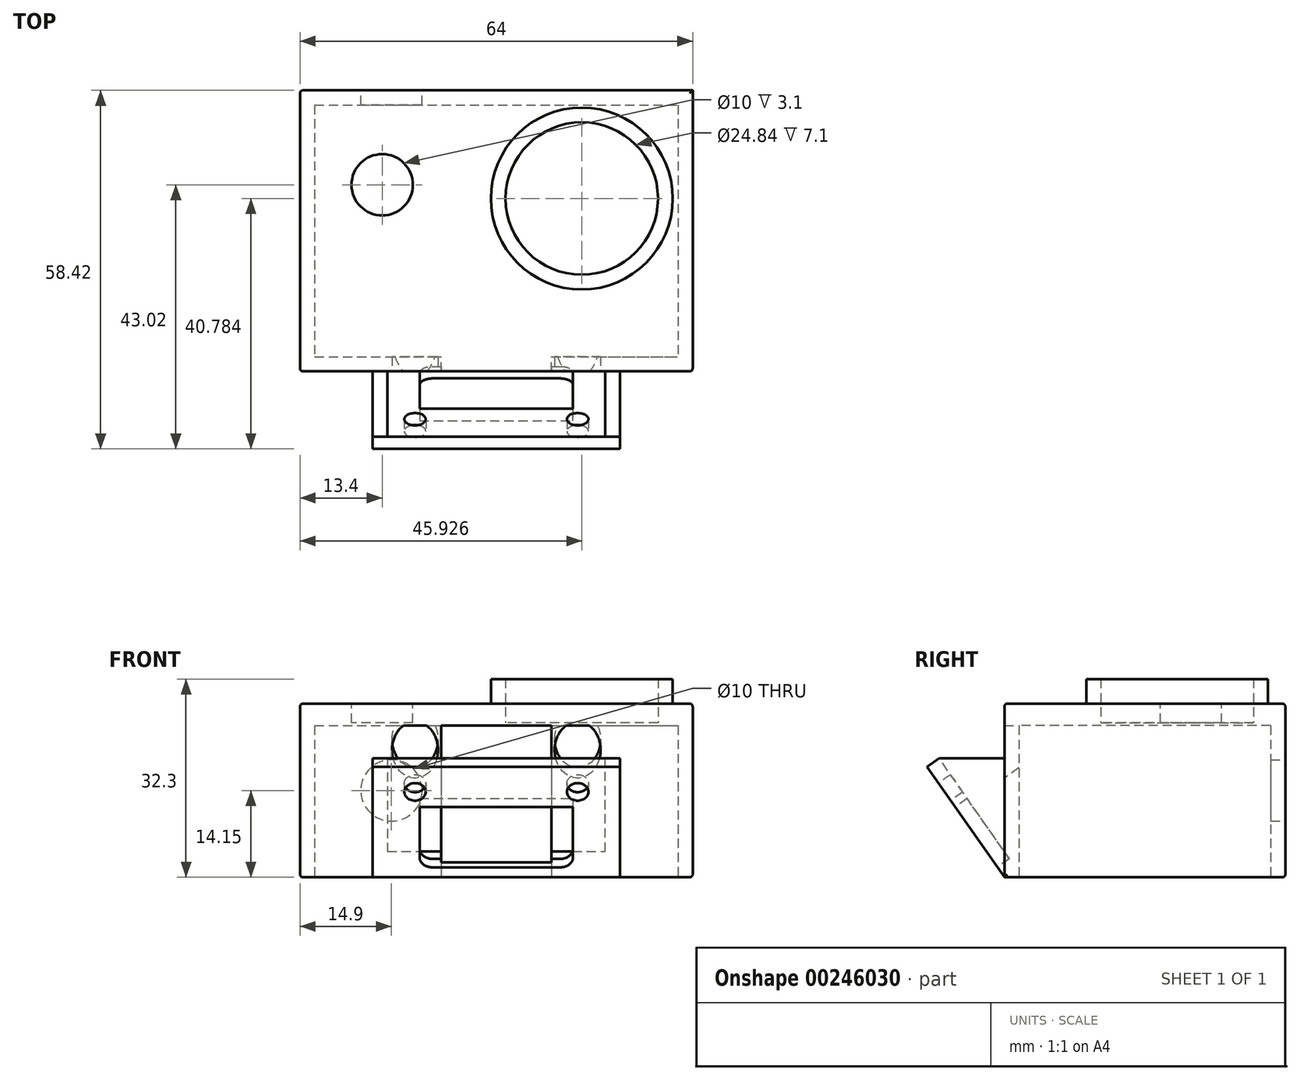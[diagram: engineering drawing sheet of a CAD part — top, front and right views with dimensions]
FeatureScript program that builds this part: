
annotation { "Feature Type Name" : "Feature", "Feature Type Description" : "" }
export const myFeature = defineFeature(function(context is Context, id is Id, definition is map)
    precondition{}
    {
        {
            assignVariable(context, id + "F0", {"name" : "goproThickness", "anyValue" : 24.7});
        }
        {
            assignVariable(context, id + "F1", {"name" : "lensDepth", "anyValue" : 4});
        }
        {
            assignVariable(context, id + "F2", {"name" : "caseThickness", "anyValue" : 2.4});
        }
        {
            assignVariable(context, id + "F3", {"name" : "webThickness", "anyValue" : 0.5});
        }
        {
            assignVariable(context, id + "F4", {"name" : "cameraTilt", "anyValue" : 35});
        }
        {
            var Q0;
            Q0=qCreatedBy(makeId("Top.planeOp"),FACE);
            var sketch = newSketch(context, id + "F5", { "sketchPlane" : qUnion([Q0])});
            skLineSegment(sketch, "E0.bottom", {"start": v(-29.6, 20.5) * mm, "end": v(29.6, 20.5) * mm});
            skLineSegment(sketch, "E0.top", {"start": v(-29.6, -20.5) * mm, "end": v(29.6, -20.5) * mm});
            skLineSegment(sketch, "E0.left", {"start": v(-29.6, 20.5) * mm, "end": v(-29.6, -20.5) * mm});
            skLineSegment(sketch, "E0.right", {"start": v(29.6, 20.5) * mm, "end": v(29.6, -20.5) * mm});
            skPoint(sketch, "E0.middle", {"position": v(0, 0) * mm});
            skLineSegment(sketch, "E1.0", {"start": v(-32, 22.9) * mm, "end": v(32, 22.9) * mm});
            skLineSegment(sketch, "E1.1", {"start": v(-32, 22.9) * mm, "end": v(-32, -22.9) * mm});
            skLineSegment(sketch, "E1.2", {"start": v(-32, -22.9) * mm, "end": v(32, -22.9) * mm});
            skLineSegment(sketch, "E1.3", {"start": v(32, 22.9) * mm, "end": v(32, -22.9) * mm});
            skSolve(sketch);
        }
        {
            var Q0;
            Q0=qSketchRegion(id+"F5",true);
            extrude(context, id + "F6", {"entities" : qUnion([Q0]), "depth" : (getVariable(context, 'goproThickness')) * mm});
        }
        {
            var Q0;
            Q0=makeQuery(id+"F6.opExtrude","CAP_FACE",FACE,{"disambiguationData":[OSD([sQuery(id+"F5.wireOp",EDGE,"E0.bottom"),sQuery(id+"F5.wireOp",EDGE,"E0.top"),sQuery(id+"F5.wireOp",EDGE,"E0.left"),sQuery(id+"F5.wireOp",EDGE,"E0.right"),sQuery(id+"F5.wireOp",EDGE,"E1.0"),sQuery(id+"F5.wireOp",EDGE,"E1.1"),sQuery(id+"F5.wireOp",EDGE,"E1.2"),sQuery(id+"F5.wireOp",EDGE,"E1.3")])],"isStart":false});
            var sketch = newSketch(context, id + "F7", { "sketchPlane" : qUnion([Q0])});
            skLineSegment(sketch, "E2.bottom", {"start": v(-29.6, 20.5) * mm, "end": v(29.6, 20.5) * mm});
            skLineSegment(sketch, "E2.top", {"start": v(-29.6, -20.5) * mm, "end": v(29.6, -20.5) * mm});
            skLineSegment(sketch, "E2.left", {"start": v(-29.6, 20.5) * mm, "end": v(-29.6, -20.5) * mm});
            skLineSegment(sketch, "E2.right", {"start": v(29.6, 20.5) * mm, "end": v(29.6, -20.5) * mm});
            skPoint(sketch, "E2.middle", {"position": v(0, 0) * mm});
            skLineSegment(sketch, "E3.bottom", {"start": v(-32, 22.9) * mm, "end": v(32, 22.9) * mm});
            skLineSegment(sketch, "E3.top", {"start": v(-32, -22.9) * mm, "end": v(32, -22.9) * mm});
            skLineSegment(sketch, "E3.left", {"start": v(-32, 22.9) * mm, "end": v(-32, -22.9) * mm});
            skLineSegment(sketch, "E3.right", {"start": v(32, 22.9) * mm, "end": v(32, -22.9) * mm});
            skSolve(sketch);
        }
        {
            var Q0;
            Q0=qSketchRegion(id+"F7",true);
            var Q1;
            Q1=makeQuery(id+"F7.imprint","IMPRINT",FACE,{"disambiguationData":[TD([[makeQuery(id+"F7.imprint","IMPRINT",EDGE,{"derivedFrom":sQuery(id+"F7.wireOp",EDGE,"E2.bottom")}),-1.0]])]});
            extrude(context, id + "F8", {"entities" : qUnion([Q0, Q1]), "operationType" : NewBodyOperationType.ADD, "depth" : (getVariable(context, 'caseThickness') * 1.5) * mm});
        }
        {
            var Q0;
            Q0=makeQuery(id+"F8.opExtrude","CAP_FACE",FACE,{"disambiguationData":[OSD([sQuery(id+"F7.wireOp",EDGE,"E3.bottom"),sQuery(id+"F7.wireOp",EDGE,"E3.top"),sQuery(id+"F7.wireOp",EDGE,"E3.left"),sQuery(id+"F7.wireOp",EDGE,"E3.right")])],"isStart":false});
            var sketch = newSketch(context, id + "F9", { "sketchPlane" : qUnion([Q0])});
            skCircle(sketch, "E4", {"center": v(-18.6, 7.5) * mm, "radius": 5 * mm});
            skSolve(sketch);
        }
        {
            var Q0;
            Q0=qSketchRegion(id+"F9",true);
            extrude(context, id + "F10", {"entities" : qUnion([Q0]), "operationType" : NewBodyOperationType.REMOVE, "oppositeDirection" : true, "depth" : (getVariable(context, 'caseThickness') * 1.5 - getVariable(context, 'webThickness')) * mm});
        }
        {
            var Q0;
            Q0=makeQuery(id+"F8.opExtrude","CAP_FACE",FACE,{"disambiguationData":[OSD([sQuery(id+"F7.wireOp",EDGE,"E3.bottom"),sQuery(id+"F7.wireOp",EDGE,"E3.top"),sQuery(id+"F7.wireOp",EDGE,"E3.left"),sQuery(id+"F7.wireOp",EDGE,"E3.right")])],"isStart":false});
            var sketch = newSketch(context, id + "F11", { "sketchPlane" : qUnion([Q0])});
            skCircle(sketch, "E5", {"center": v(13.93, 5.26) * mm, "radius": 12.42 * mm});
            skCircle(sketch, "E6", {"center": v(13.93, 5.26) * mm, "radius": 14.82 * mm});
            skSolve(sketch);
        }
        {
            var Q0;
            Q0=qSketchRegion(id+"F11",true);
            extrude(context, id + "F12", {"entities" : qUnion([Q0]), "operationType" : NewBodyOperationType.ADD, "depth" : (getVariable(context, 'lensDepth')) * mm});
        }
        {
            var Q0;
            Q0=makeQuery(id+"F12.boolean.opBoolean","SPLIT",FACE,{"disambiguationData":[TD([makeQuery(id+"F12.opExtrude","SWEPT_FACE",FACE,{"disambiguationData":[OSD([sQuery(id+"F11.wireOp",EDGE,"E5")])]})])],"derivedFrom":makeQuery(id+"F8.opExtrude","CAP_FACE",FACE,{"disambiguationData":[OSD([sQuery(id+"F7.wireOp",EDGE,"E3.bottom"),sQuery(id+"F7.wireOp",EDGE,"E3.top"),sQuery(id+"F7.wireOp",EDGE,"E3.left"),sQuery(id+"F7.wireOp",EDGE,"E3.right")])],"isStart":false})});
            extrude(context, id + "F13", {"entities" : qUnion([Q0]), "operationType" : NewBodyOperationType.REMOVE, "oppositeDirection" : true, "depth" : (getVariable(context, 'caseThickness') * 1.5 - getVariable(context, 'webThickness')) * mm});
        }
        {
            var Q0;
            Q0=makeQuery(id+"F8.boolean.opBoolean","MERGE",FACE,{"derivedFrom":[makeQuery(id+"F6.opExtrude","SWEPT_FACE",FACE,{"disambiguationData":[OSD([sQuery(id+"F5.wireOp",EDGE,"E1.0")])]}),makeQuery(id+"F8.opExtrude","SWEPT_FACE",FACE,{"disambiguationData":[OSD([sQuery(id+"F7.wireOp",EDGE,"E3.bottom")])]})]});
            var sketch = newSketch(context, id + "F14", { "sketchPlane" : qUnion([Q0])});
            skCircle(sketch, "E7", {"center": v(17.1, 14.15) * mm, "radius": 5 * mm});
            skPoint(sketch, "E7.centerSnap0", {"position": v(32, 14.15) * mm});
            skSolve(sketch);
        }
        {
            var Q0;
            Q0=qSketchRegion(id+"F14",true);
            extrude(context, id + "F15", {"entities" : qUnion([Q0]), "operationType" : NewBodyOperationType.REMOVE, "oppositeDirection" : true, "depth" : (getVariable(context, 'caseThickness')) * mm});
        }
        {
            var Q0;
            Q0=makeQuery(id+"F6.opExtrude","CAP_EDGE",EDGE,{"disambiguationData":[OSD([sQuery(id+"F5.wireOp",EDGE,"E1.2")])],"isStart":true});
            cPlane(context, id + "F16", {"entities" : qUnion([Q0]), "cplaneType" : CPlaneType.LINE_ANGLE, "offset" : 25 * mm, "angle" : (getVariable(context, 'cameraTilt')) * degree, "width" : 150 * mm, "height" : 150 * mm});
        }
        {
            var Q0;
            Q0=qCreatedBy(id+"F16.planeOp",FACE);
            var sketch = newSketch(context, id + "F17", { "sketchPlane" : qUnion([Q0])});
            skLineSegment(sketch, "E8", {"start": v(0, 13.13) * mm, "end": v(17.75, 13.13) * mm});
            skLineSegment(sketch, "E9", {"start": v(17.75, 13.13) * mm, "end": v(17.75, 35.13) * mm});
            skLineSegment(sketch, "E10", {"start": v(17.75, 35.13) * mm, "end": v(-17.75, 35.13) * mm});
            skLineSegment(sketch, "E11", {"start": v(-17.75, 35.13) * mm, "end": v(-17.75, 13.13) * mm});
            skLineSegment(sketch, "E12", {"start": v(-17.75, 13.13) * mm, "end": v(0, 13.13) * mm});
            skLineSegment(sketch, "E13", {"start": v(0, 35.13) * mm, "end": v(0, 24.13) * mm});
            skPoint(sketch, "E13.endSnap0", {"position": v(17.75, 24.13) * mm});
            skLineSegment(sketch, "E14", {"start": v(0, 24.13) * mm, "end": v(0, 13.13) * mm});
            skCircle(sketch, "E15", {"center": v(13.25, 30.13) * mm, "radius": 1.75 * mm});
            skCircle(sketch, "E16.MirrorC", {"center": v(-13.25, 30.13) * mm, "radius": 1.75 * mm});
            skSolve(sketch);
        }
        {
            var Q0;
            Q0=makeQuery(id+"F17.imprint","IMPRINT",FACE,{"disambiguationData":[TD([[makeQuery(id+"F17.imprint","IMPRINT",EDGE,{"derivedFrom":sQuery(id+"F17.wireOp",EDGE,"E8")}),1.0]])]});
            var Q1;
            {var subQ0=sQuery(id+"F17.wireOp",EDGE,"E11");Q1=makeQuery(id+"F17.imprint","IMPRINT",FACE,{"disambiguationData":[TD([[makeQuery(id+"F17.imprint","IMPRINT",EDGE,{"derivedFrom":subQ0}),1.0]])]});}
            extrude(context, id + "F18", {"entities" : qUnion([Q0, Q1]), "operationType" : NewBodyOperationType.ADD, "depth" : (getVariable(context, 'caseThickness')) * mm});
        }
        {
            var Q0;
            Q0=makeQuery(id+"F18.opExtrude","SWEPT_FACE",FACE,{"disambiguationData":[OSD([sQuery(id+"F17.wireOp",EDGE,"E9")])]});
            var sketch = newSketch(context, id + "F19", { "sketchPlane" : qUnion([Q0])});
            skLineSegment(sketch, "E17", {"start": v(35.52, 18.02) * mm, "end": v(33.55, 19.4) * mm});
            skLineSegment(sketch, "E18", {"start": v(22.9, 0) * mm, "end": v(35.52, 18.02) * mm});
            skLineSegment(sketch, "E19", {"start": v(33.55, 19.4) * mm, "end": v(22.9, 19.4) * mm});
            skLineSegment(sketch, "E20", {"start": v(22.9, 19.4) * mm, "end": v(22.9, 0) * mm});
            skSolve(sketch);
        }
        {
            var Q0;
            Q0=qSketchRegion(id+"F19",true);
            extrude(context, id + "F20", {"entities" : qUnion([Q0]), "operationType" : NewBodyOperationType.ADD, "depth" : (getVariable(context, 'caseThickness')) * mm});
        }
        {
            var Q0;
            Q0=makeQuery(id+"F18.opExtrude","SWEPT_FACE",FACE,{"disambiguationData":[OSD([sQuery(id+"F17.wireOp",EDGE,"E11")])]});
            var sketch = newSketch(context, id + "F21", { "sketchPlane" : qUnion([Q0])});
            skLineSegment(sketch, "E21", {"start": v(-22.9, 0) * mm, "end": v(-35.52, 18.02) * mm});
            skLineSegment(sketch, "E22", {"start": v(-35.52, 18.02) * mm, "end": v(-33.55, 19.4) * mm});
            skLineSegment(sketch, "E23", {"start": v(-33.55, 19.4) * mm, "end": v(-22.9, 19.4) * mm});
            skLineSegment(sketch, "E24", {"start": v(-22.9, 19.4) * mm, "end": v(-22.9, 0) * mm});
            skSolve(sketch);
        }
        {
            var Q0;
            Q0=qSketchRegion(id+"F21",true);
            extrude(context, id + "F22", {"entities" : qUnion([Q0]), "operationType" : NewBodyOperationType.ADD, "depth" : (getVariable(context, 'caseThickness')) * mm});
        }
        {
            var Q0;
            Q0=makeQuery(id+"F22.boolean.opBoolean","MERGE",FACE,{"derivedFrom":[makeQuery(id+"F20.boolean.opBoolean","MERGE",FACE,{"derivedFrom":[makeQuery(id+"F18.opExtrude","CAP_FACE",FACE,{"disambiguationData":[OSD([sQuery(id+"F17.wireOp",EDGE,"E8"),sQuery(id+"F17.wireOp",EDGE,"E9"),sQuery(id+"F17.wireOp",EDGE,"E10"),sQuery(id+"F17.wireOp",EDGE,"E11"),sQuery(id+"F17.wireOp",EDGE,"E12"),sQuery(id+"F17.wireOp",EDGE,"E15"),sQuery(id+"F17.wireOp",EDGE,"E16.MirrorC")])],"isStart":true}),makeQuery(id+"F20.opExtrude","SWEPT_FACE",FACE,{"disambiguationData":[OSD([sQuery(id+"F19.wireOp",EDGE,"E18")])]})]}),makeQuery(id+"F22.opExtrude","SWEPT_FACE",FACE,{"disambiguationData":[OSD([sQuery(id+"F21.wireOp",EDGE,"E21")])]})]});
            var sketch = newSketch(context, id + "F23", { "sketchPlane" : qUnion([Q0])});
            skCircle(sketch, "E25", {"center": v(-13.25, 30.13) * mm, "radius": 1.75 * mm});
            skCircle(sketch, "E26.MirrorC", {"center": v(13.25, 30.13) * mm, "radius": 1.75 * mm});
            skSolve(sketch);
        }
        {
            var Q0;
            Q0=qSketchRegion(id+"F23",true);
            var Q1;
            Q1=makeQuery(id+"F8.opExtrude","CAP_FACE",FACE,{"disambiguationData":[OSD([sQuery(id+"F7.wireOp",EDGE,"E3.bottom"),sQuery(id+"F7.wireOp",EDGE,"E3.top"),sQuery(id+"F7.wireOp",EDGE,"E3.left"),sQuery(id+"F7.wireOp",EDGE,"E3.right")])],"isStart":true});
            extrude(context, id + "F24", {"entities" : qUnion([Q0]), "operationType" : NewBodyOperationType.REMOVE, "endBound" : BoundingType.UP_TO_SURFACE, "oppositeDirection" : true, "endBoundEntityFace" : qUnion([Q1]), "depth" : 25 * mm});
        }
        {
            var Q0;
            Q0=makeQuery(id+"F8.opExtrude","CAP_EDGE",EDGE,{"disambiguationData":[OSD([sQuery(id+"F7.wireOp",EDGE,"E3.left")])],"isStart":false});
            var Q1;
            Q1=makeQuery(id+"F8.opExtrude","CAP_EDGE",EDGE,{"disambiguationData":[OSD([sQuery(id+"F7.wireOp",EDGE,"E3.top")])],"isStart":false});
            var Q2;
            Q2=makeQuery(id+"F8.opExtrude","CAP_EDGE",EDGE,{"disambiguationData":[OSD([sQuery(id+"F7.wireOp",EDGE,"E3.right")])],"isStart":false});
            var Q3;
            Q3=makeQuery(id+"F8.opExtrude","CAP_EDGE",EDGE,{"disambiguationData":[OSD([sQuery(id+"F7.wireOp",EDGE,"E3.bottom")])],"isStart":false});
            var Q4;
            Q4=makeQuery(id+"F10.boolean.opBoolean","COPY",EDGE,{"derivedFrom":makeQuery(id+"F10.opExtrude","CAP_EDGE",EDGE,{"disambiguationData":[OSD([sQuery(id+"F9.wireOp",EDGE,"E4")])],"isStart":true})});
            var Q5;
            Q5=makeQuery(id+"F6.opExtrude","CAP_EDGE",EDGE,{"disambiguationData":[OSD([sQuery(id+"F5.wireOp",EDGE,"E1.3")])],"isStart":true});
            var Q6;
            Q6=makeQuery(id+"F6.opExtrude","CAP_EDGE",EDGE,{"disambiguationData":[OSD([sQuery(id+"F5.wireOp",EDGE,"E1.0")])],"isStart":true});
            var Q7;
            Q7=makeQuery(id+"F8.boolean.opBoolean","MERGE",EDGE,{"derivedFrom":[makeQuery(id+"F6.opExtrude","SWEPT_EDGE",EDGE,{"disambiguationData":[OSD([sQuery(id+"F5.wireOp",EDGE,"E1.0"),sQuery(id+"F5.wireOp",EDGE,"E1.1")])]}),makeQuery(id+"F8.opExtrude","SWEPT_EDGE",EDGE,{"disambiguationData":[OSD([sQuery(id+"F7.wireOp",EDGE,"E3.bottom"),sQuery(id+"F7.wireOp",EDGE,"E3.left")])]})]});
            var Q8;
            Q8=makeQuery(id+"F6.opExtrude","CAP_EDGE",EDGE,{"disambiguationData":[OSD([sQuery(id+"F5.wireOp",EDGE,"E1.1")])],"isStart":true});
            var Q9;
            Q9=makeQuery(id+"F8.boolean.opBoolean","MERGE",EDGE,{"derivedFrom":[makeQuery(id+"F6.opExtrude","SWEPT_EDGE",EDGE,{"disambiguationData":[OSD([sQuery(id+"F5.wireOp",EDGE,"E1.1"),sQuery(id+"F5.wireOp",EDGE,"E1.2")])]}),makeQuery(id+"F8.opExtrude","SWEPT_EDGE",EDGE,{"disambiguationData":[OSD([sQuery(id+"F7.wireOp",EDGE,"E3.top"),sQuery(id+"F7.wireOp",EDGE,"E3.left")])]})]});
            var Q10;
            Q10=makeQuery(id+"F8.boolean.opBoolean","MERGE",EDGE,{"derivedFrom":[makeQuery(id+"F6.opExtrude","SWEPT_EDGE",EDGE,{"disambiguationData":[OSD([sQuery(id+"F5.wireOp",EDGE,"E1.2"),sQuery(id+"F5.wireOp",EDGE,"E1.3")])]}),makeQuery(id+"F8.opExtrude","SWEPT_EDGE",EDGE,{"disambiguationData":[OSD([sQuery(id+"F7.wireOp",EDGE,"E3.top"),sQuery(id+"F7.wireOp",EDGE,"E3.right")])]})]});
            fillet(context, id + "F25", {"entities" : qUnion([Q0, Q1, Q2, Q3, Q4, Q5, Q6, Q7, Q8, Q9, Q10]), "radius" : 0.5 * mm, "tangentPropagation" : true, "allowEdgeOverflow" : false});
        }
        {
            var Q0;
            Q0=makeQuery(id+"F6.opExtrude","CAP_FACE",FACE,{"disambiguationData":[OSD([sQuery(id+"F5.wireOp",EDGE,"E0.bottom"),sQuery(id+"F5.wireOp",EDGE,"E0.top"),sQuery(id+"F5.wireOp",EDGE,"E0.left"),sQuery(id+"F5.wireOp",EDGE,"E0.right"),sQuery(id+"F5.wireOp",EDGE,"E1.0"),sQuery(id+"F5.wireOp",EDGE,"E1.1"),sQuery(id+"F5.wireOp",EDGE,"E1.2"),sQuery(id+"F5.wireOp",EDGE,"E1.3")])],"isStart":true});
            var sketch = newSketch(context, id + "F26", { "sketchPlane" : qUnion([Q0])});
            skLineSegment(sketch, "E27.bottom", {"start": v(-9, 22.9) * mm, "end": v(9, 22.9) * mm});
            skLineSegment(sketch, "E27.top", {"start": v(-9, 20.5) * mm, "end": v(9, 20.5) * mm});
            skLineSegment(sketch, "E27.left", {"start": v(-9, 22.9) * mm, "end": v(-9, 20.5) * mm});
            skLineSegment(sketch, "E27.right", {"start": v(9, 22.9) * mm, "end": v(9, 20.5) * mm});
            skPoint(sketch, "E27.middle", {"position": v(0, 21.7) * mm});
            skSolve(sketch);
        }
        {
            var Q0;
            Q0=qSketchRegion(id+"F26",true);
            var Q1;
            Q1=makeQuery(id+"F8.opExtrude","CAP_FACE",FACE,{"disambiguationData":[OSD([sQuery(id+"F7.wireOp",EDGE,"E3.bottom"),sQuery(id+"F7.wireOp",EDGE,"E3.top"),sQuery(id+"F7.wireOp",EDGE,"E3.left"),sQuery(id+"F7.wireOp",EDGE,"E3.right")])],"isStart":true});
            extrude(context, id + "F27", {"entities" : qUnion([Q0]), "operationType" : NewBodyOperationType.REMOVE, "endBound" : BoundingType.UP_TO_SURFACE, "oppositeDirection" : true, "endBoundEntityFace" : qUnion([Q1]), "depth" : 25 * mm});
        }
        {
            var Q0;
            Q0=makeQuery(id+"F18.opExtrude","CAP_FACE",FACE,{"disambiguationData":[OSD([sQuery(id+"F17.wireOp",EDGE,"E8"),sQuery(id+"F17.wireOp",EDGE,"E9"),sQuery(id+"F17.wireOp",EDGE,"E10"),sQuery(id+"F17.wireOp",EDGE,"E11"),sQuery(id+"F17.wireOp",EDGE,"E12"),sQuery(id+"F17.wireOp",EDGE,"E15"),sQuery(id+"F17.wireOp",EDGE,"E16.MirrorC")])],"isStart":false});
            var sketch = newSketch(context, id + "F28", { "sketchPlane" : qUnion([Q0])});
            skCircle(sketch, "E28", {"center": v(13.25, 30.13) * mm, "radius": 3.75 * mm});
            skCircle(sketch, "E29.MirrorC", {"center": v(-13.25, 30.13) * mm, "radius": 3.75 * mm});
            skSolve(sketch);
        }
        {
            var Q0;
            Q0=qSketchRegion(id+"F28",true);
            var Q1;
            {var subQ0=sQuery(id+"F7.wireOp",EDGE,"E3.right");var subQ1=sQuery(id+"F7.wireOp",EDGE,"E3.left");var subQ2=sQuery(id+"F7.wireOp",EDGE,"E3.top");var subQ3=sQuery(id+"F7.wireOp",EDGE,"E3.bottom");Q1=makeQuery(id+"F27.boolean.opBoolean","MERGE",FACE,{"derivedFrom":[makeQuery(id+"F8.opExtrude","CAP_FACE",FACE,{"disambiguationData":[OSD([subQ3,subQ2,subQ1,subQ0])],"isStart":true}),makeQuery(id+"F27.opExtrude","CAP_FACE",FACE,{"disambiguationData":[OSD([subQ3,subQ2,subQ1,subQ0])],"isStart":false})]});}
            extrude(context, id + "F29", {"entities" : qUnion([Q0]), "operationType" : NewBodyOperationType.REMOVE, "endBound" : BoundingType.UP_TO_SURFACE, "endBoundEntityFace" : qUnion([Q1]), "depth" : 25 * mm});
        }
        {
            var Q0;
            Q0=makeQuery(id+"F22.boolean.opBoolean","MERGE",FACE,{"derivedFrom":[makeQuery(id+"F20.boolean.opBoolean","MERGE",FACE,{"derivedFrom":[makeQuery(id+"F18.opExtrude","CAP_FACE",FACE,{"disambiguationData":[OSD([sQuery(id+"F17.wireOp",EDGE,"E8"),sQuery(id+"F17.wireOp",EDGE,"E9"),sQuery(id+"F17.wireOp",EDGE,"E10"),sQuery(id+"F17.wireOp",EDGE,"E11"),sQuery(id+"F17.wireOp",EDGE,"E12"),sQuery(id+"F17.wireOp",EDGE,"E15"),sQuery(id+"F17.wireOp",EDGE,"E16.MirrorC")])],"isStart":true}),makeQuery(id+"F20.opExtrude","SWEPT_FACE",FACE,{"disambiguationData":[OSD([sQuery(id+"F19.wireOp",EDGE,"E18")])]})]}),makeQuery(id+"F22.opExtrude","SWEPT_FACE",FACE,{"disambiguationData":[OSD([sQuery(id+"F21.wireOp",EDGE,"E21")])]})]});
            var sketch = newSketch(context, id + "F30", { "sketchPlane" : qUnion([Q0])});
            skPoint(sketch, "E30", {"position": v(-13.25, 30.13) * mm});
            skPoint(sketch, "E31", {"position": v(13.25, 30.13) * mm});
            skLineSegment(sketch, "E32", {"start": v(-12.5, 15.13) * mm, "end": v(0, 15.13) * mm});
            skLineSegment(sketch, "E33", {"start": v(0, 15.13) * mm, "end": v(12.5, 15.13) * mm});
            skLineSegment(sketch, "E34", {"start": v(-12.5, 15.13) * mm, "end": v(-12.5, 27.13) * mm});
            skLineSegment(sketch, "E35", {"start": v(-12.5, 27.13) * mm, "end": v(12.5, 27.13) * mm});
            skLineSegment(sketch, "E36", {"start": v(12.5, 27.13) * mm, "end": v(12.5, 15.13) * mm});
            skSolve(sketch);
        }
        {
            var Q0;
            Q0=qSketchRegion(id+"F30",true);
            var Q1;
            {var subQ1=sQuery(id+"F30.wireOp",EDGE,"BaOD2BEO-CHPW-Bun6-DBrZ-VnkcG4sa4ueP");Q1=makeQuery(id+"F30.imprint","IMPRINT",FACE,{"disambiguationData":[TD([[makeQuery(id+"F30.imprint","IMPRINT",EDGE,{"derivedFrom":subQ1}),1.0]])]});}
            extrude(context, id + "F31", {"entities" : qUnion([Q0, Q1]), "operationType" : NewBodyOperationType.REMOVE, "oppositeDirection" : true, "depth" : (getVariable(context, 'caseThickness')) * mm});
        }
        {
            var Q0;
            Q0=makeQuery(id+"F31.boolean.opBoolean","COPY",EDGE,{"derivedFrom":makeQuery(id+"F31.opExtrude","SWEPT_EDGE",EDGE,{"disambiguationData":[OSD([sQuery(id+"F30.wireOp",EDGE,"lFEBneSN-Pb8Z-hWur-7Ffs-Kk0kVPCbnb5V"),sQuery(id+"F30.wireOp",EDGE,"E32")])]})});
            var Q1;
            Q1=makeQuery(id+"F31.boolean.opBoolean","COPY",EDGE,{"derivedFrom":makeQuery(id+"F31.opExtrude","SWEPT_EDGE",EDGE,{"disambiguationData":[OSD([sQuery(id+"F30.wireOp",EDGE,"E33"),sQuery(id+"F30.wireOp",EDGE,"hKJfBmfI-InRr-J8dV-goCd-TeNdGNQ7apCS")])]})});
            fillet(context, id + "F32", {"entities" : qUnion([Q0, Q1]), "radius" : 2 * mm, "tangentPropagation" : true, "allowEdgeOverflow" : false});
        }
        {
            var Q0;
            Q0=makeQuery(id+"F12.opExtrude","CAP_FACE",FACE,{"disambiguationData":[OSD([sQuery(id+"F11.wireOp",EDGE,"E5"),sQuery(id+"F11.wireOp",EDGE,"E6")])],"isStart":false});
            cPlane(context, id + "F33", {"entities" : qUnion([Q0]), "cplaneType" : CPlaneType.OFFSET, "offset" : 0 * mm, "width" : 150 * mm, "height" : 150 * mm});
        }
    });
